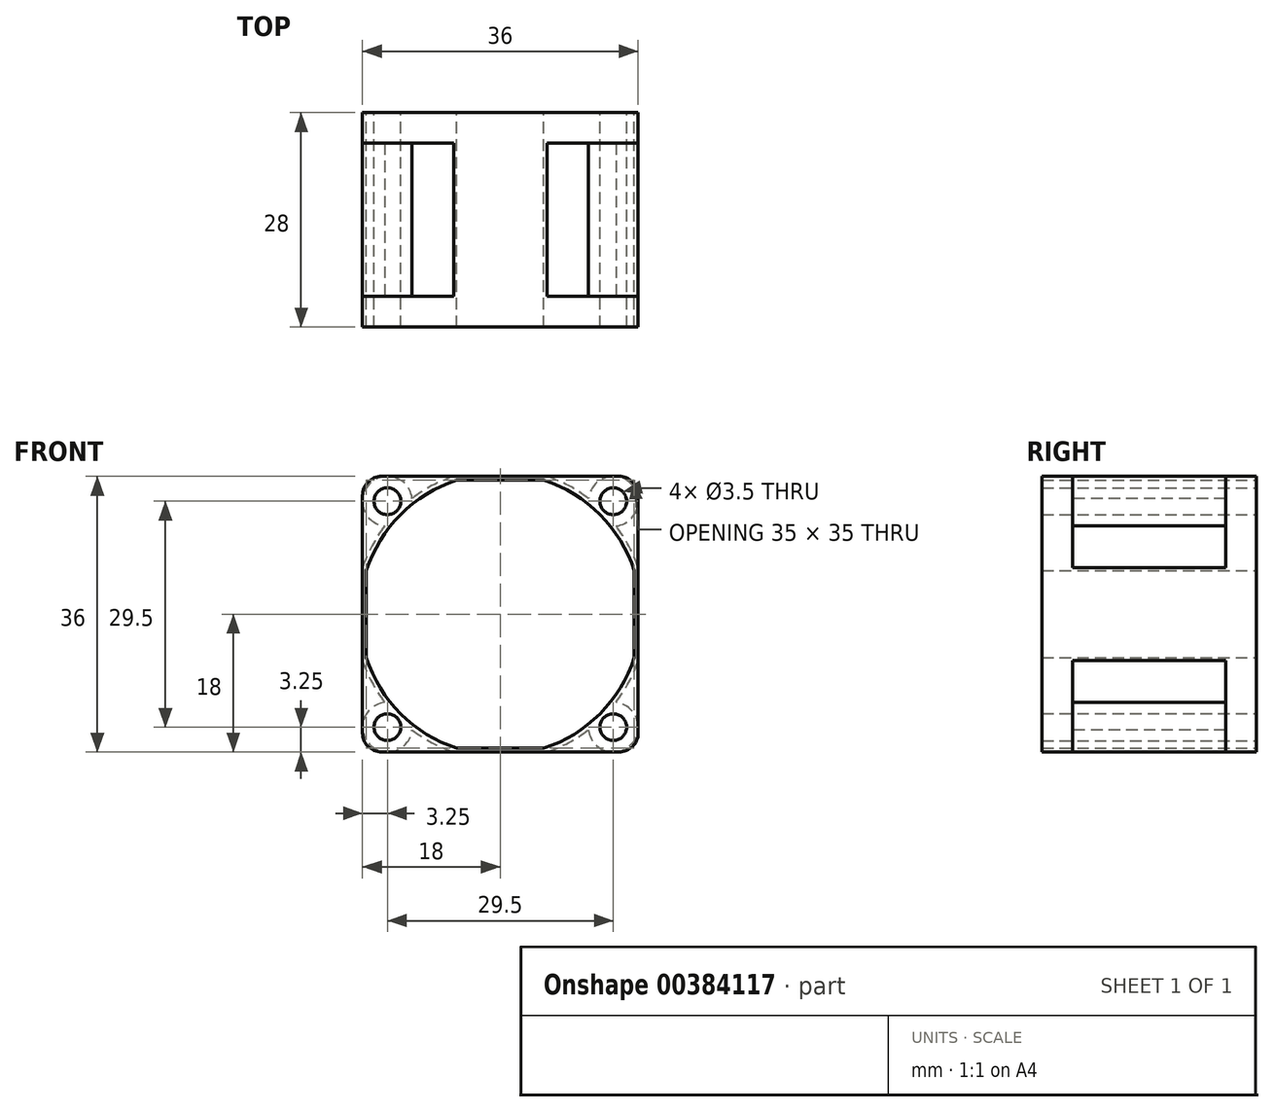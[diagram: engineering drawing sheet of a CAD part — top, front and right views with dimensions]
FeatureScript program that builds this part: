
annotation { "Feature Type Name" : "Feature", "Feature Type Description" : "" }
export const myFeature = defineFeature(function(context is Context, id is Id, definition is map)
    precondition{}
    {
        {
            var Q0;
            Q0=qCreatedBy(makeId("Front.planeOp"),FACE);
            var sketch = newSketch(context, id + "F0", { "sketchPlane" : qUnion([Q0])});
            skLineSegment(sketch, "E0.bottom", {"start": v(-18, 18) * mm, "end": v(18, 18) * mm});
            skLineSegment(sketch, "E0.top", {"start": v(-18, -18) * mm, "end": v(18, -18) * mm});
            skLineSegment(sketch, "E0.left", {"start": v(-18, 18) * mm, "end": v(-18, -18) * mm});
            skLineSegment(sketch, "E0.right", {"start": v(18, 18) * mm, "end": v(18, -18) * mm});
            skArc(sketch, "E1", {"start": v(-5.68, 17.5) * mm, "mid": v(-13.01, 13.01) * mm, "end": v(-17.5, 5.68) * mm});
            skCircle(sketch, "E2", {"center": v(0, 0) * mm, "radius": 17.5 * mm, "construction": true});
            skLineSegment(sketch, "E3", {"start": v(0, 22.42) * mm, "end": v(0, -25.75) * mm, "construction": true});
            skLineSegment(sketch, "E4", {"start": v(-21.61, 0) * mm, "end": v(23.43, 0) * mm, "construction": true});
            skLineSegment(sketch, "E5", {"start": v(-22.47, 22.47) * mm, "end": v(21.99, -21.99) * mm, "construction": true});
            skLineSegment(sketch, "E6", {"start": v(22.36, 22.36) * mm, "end": v(-20.46, -20.46) * mm, "construction": true});
            skCircle(sketch, "E7", {"center": v(-14.75, 14.75) * mm, "radius": 1.75 * mm});
            skCircle(sketch, "E8", {"center": v(14.75, 14.75) * mm, "radius": 1.75 * mm});
            skCircle(sketch, "E9", {"center": v(14.75, -14.75) * mm, "radius": 1.75 * mm});
            skCircle(sketch, "E10", {"center": v(-14.75, -14.75) * mm, "radius": 1.75 * mm});
            skLineSegment(sketch, "E11", {"start": v(-5.68, 17.5) * mm, "end": v(5.68, 17.5) * mm});
            skLineSegment(sketch, "E12", {"start": v(-5.68, -17.5) * mm, "end": v(5.68, -17.5) * mm});
            skLineSegment(sketch, "E13", {"start": v(17.5, 5.68) * mm, "end": v(17.5, -5.68) * mm});
            skLineSegment(sketch, "E14", {"start": v(-17.5, 5.68) * mm, "end": v(-17.5, -5.68) * mm});
            skArc(sketch, "E15.trimOffspring", {"start": v(-17.5, -5.68) * mm, "mid": v(-13.01, -13.01) * mm, "end": v(-5.68, -17.5) * mm});
            skArc(sketch, "E16.trimOffspring", {"start": v(5.68, -17.5) * mm, "mid": v(13.01, -13.01) * mm, "end": v(17.5, -5.68) * mm});
            skArc(sketch, "E17.trimOffspring", {"start": v(17.5, 5.68) * mm, "mid": v(13.01, 13.01) * mm, "end": v(5.68, 17.5) * mm});
            skSolve(sketch);
        }
        {
            var Q0;
            Q0 = qSketchRegion(id + "F0", true);
            extrude(context, id + "F1", {"entities" : qUnion([Q0]), "depth" : 28 * mm, "symmetric" : true});
        }
        {
            var Q0;
            Q0=qCreatedBy(makeId("Front.planeOp"),FACE);
            var sketch = newSketch(context, id + "F2", { "sketchPlane" : qUnion([Q0])});
            skArc(sketch, "E18", {"start": v(-11.52, 15.1) * mm, "mid": v(-17.05, 17.05) * mm, "end": v(-15.1, 11.52) * mm});
            skArc(sketch, "E19", {"start": v(-15.1, 11.52) * mm, "mid": v(-16.78, 8.92) * mm, "end": v(-18, 6.08) * mm});
            skLineSegment(sketch, "E20", {"start": v(19, 19) * mm, "end": v(6.08, 19) * mm});
            skLineSegment(sketch, "E21", {"start": v(-19, 19) * mm, "end": v(-19, 6.08) * mm});
            skLineSegment(sketch, "E22", {"start": v(-19, -19) * mm, "end": v(-6.08, -19) * mm});
            skLineSegment(sketch, "E23", {"start": v(19, -19) * mm, "end": v(19, -6.08) * mm});
            skArc(sketch, "E24", {"start": v(15.1, 11.52) * mm, "mid": v(17.05, 17.05) * mm, "end": v(11.52, 15.1) * mm});
            skArc(sketch, "E25", {"start": v(11.52, -15.1) * mm, "mid": v(17.05, -17.05) * mm, "end": v(15.1, -11.52) * mm});
            skArc(sketch, "E26", {"start": v(-15.1, -11.52) * mm, "mid": v(-17.05, -17.05) * mm, "end": v(-11.52, -15.1) * mm});
            skArc(sketch, "E27.trimOffspring", {"start": v(11.52, 15.1) * mm, "mid": v(8.92, 16.78) * mm, "end": v(6.08, 18) * mm});
            skArc(sketch, "E28.trimOffspring", {"start": v(15.1, -11.52) * mm, "mid": v(16.78, -8.92) * mm, "end": v(18, -6.08) * mm});
            skArc(sketch, "E29.trimOffspring", {"start": v(-11.52, -15.1) * mm, "mid": v(-8.92, -16.78) * mm, "end": v(-6.08, -18) * mm});
            skLineSegment(sketch, "E30", {"start": v(-6.08, 18) * mm, "end": v(-6.08, 19) * mm});
            skLineSegment(sketch, "E31", {"start": v(6.08, 18) * mm, "end": v(6.08, 19) * mm});
            skLineSegment(sketch, "E32", {"start": v(-18, 6.08) * mm, "end": v(-19, 6.08) * mm});
            skLineSegment(sketch, "E33", {"start": v(-18, -6.08) * mm, "end": v(-19, -6.08) * mm});
            skLineSegment(sketch, "E34", {"start": v(18, 6.08) * mm, "end": v(19, 6.08) * mm});
            skLineSegment(sketch, "E35", {"start": v(18, -6.08) * mm, "end": v(19, -6.08) * mm});
            skLineSegment(sketch, "E36", {"start": v(-6.08, -18) * mm, "end": v(-6.08, -19) * mm});
            skLineSegment(sketch, "E37", {"start": v(6.08, -18) * mm, "end": v(6.08, -19) * mm});
            skArc(sketch, "E38.trimOffspring", {"start": v(-18, -6.08) * mm, "mid": v(-16.78, -8.92) * mm, "end": v(-15.1, -11.52) * mm});
            skLineSegment(sketch, "E39.trimOffspring", {"start": v(-19, -6.08) * mm, "end": v(-19, -19) * mm});
            skLineSegment(sketch, "E40.trimOffspring", {"start": v(6.08, -19) * mm, "end": v(19, -19) * mm});
            skArc(sketch, "E41.trimOffspring", {"start": v(6.08, -18) * mm, "mid": v(8.92, -16.78) * mm, "end": v(11.52, -15.1) * mm});
            skLineSegment(sketch, "E42.trimOffspring", {"start": v(19, 6.08) * mm, "end": v(19, 19) * mm});
            skArc(sketch, "E43.trimOffspring", {"start": v(18, 6.08) * mm, "mid": v(16.78, 8.92) * mm, "end": v(15.1, 11.52) * mm});
            skLineSegment(sketch, "E44.trimOffspring", {"start": v(-6.08, 19) * mm, "end": v(-19, 19) * mm});
            skArc(sketch, "E45.trimOffspring", {"start": v(-6.08, 18) * mm, "mid": v(-8.92, 16.78) * mm, "end": v(-11.52, 15.1) * mm});
            skSolve(sketch);
        }
        {
            var Q0;
            Q0 = qSketchRegion(id + "F2", true);
            extrude(context, id + "F3", {"entities" : qUnion([Q0]), "operationType" : NewBodyOperationType.REMOVE, "oppositeDirection" : true, "depth" : 20 * mm, "symmetric" : true});
        }
        {
            var Q0;
            {var subQ0=sQuery(id+"F0.wireOp",EDGE,"E0.bottom");var subQ1=sQuery(id+"F0.wireOp",EDGE,"E0.right");Q0=makeQuery(id+"F3.boolean.opBoolean","SPLIT",EDGE,{"disambiguationData":[TD([makeQuery(id+"F3.opExtrude","CAP_FACE",FACE,{"disambiguationData":[OSD([sQuery(id+"F2.wireOp",EDGE,"E20"),sQuery(id+"F2.wireOp",EDGE,"E24"),sQuery(id+"F2.wireOp",EDGE,"E27.trimOffspring"),sQuery(id+"F2.wireOp",EDGE,"E31"),sQuery(id+"F2.wireOp",EDGE,"E34"),sQuery(id+"F2.wireOp",EDGE,"E42.trimOffspring"),sQuery(id+"F2.wireOp",EDGE,"E43.trimOffspring")])],"isStart":true})])],"derivedFrom":makeQuery(id+"F1.opExtrude","SWEPT_EDGE",EDGE,{"disambiguationData":[OSD([subQ0,subQ1])]})});}
            var Q1;
            {var subQ0=sQuery(id+"F0.wireOp",EDGE,"E0.bottom");var subQ1=sQuery(id+"F0.wireOp",EDGE,"E0.right");Q1=makeQuery(id+"F3.boolean.opBoolean","SPLIT",EDGE,{"disambiguationData":[TD([makeQuery(id+"F3.opExtrude","CAP_FACE",FACE,{"disambiguationData":[OSD([sQuery(id+"F2.wireOp",EDGE,"E20"),sQuery(id+"F2.wireOp",EDGE,"E24"),sQuery(id+"F2.wireOp",EDGE,"E27.trimOffspring"),sQuery(id+"F2.wireOp",EDGE,"E31"),sQuery(id+"F2.wireOp",EDGE,"E34"),sQuery(id+"F2.wireOp",EDGE,"E42.trimOffspring"),sQuery(id+"F2.wireOp",EDGE,"E43.trimOffspring")])],"isStart":false})])],"derivedFrom":makeQuery(id+"F1.opExtrude","SWEPT_EDGE",EDGE,{"disambiguationData":[OSD([subQ0,subQ1])]})});}
            var Q2;
            {var subQ0=sQuery(id+"F0.wireOp",EDGE,"E0.right");var subQ1=sQuery(id+"F0.wireOp",EDGE,"E0.top");Q2=makeQuery(id+"F3.boolean.opBoolean","SPLIT",EDGE,{"disambiguationData":[TD([makeQuery(id+"F3.opExtrude","CAP_FACE",FACE,{"disambiguationData":[OSD([sQuery(id+"F2.wireOp",EDGE,"E23"),sQuery(id+"F2.wireOp",EDGE,"E25"),sQuery(id+"F2.wireOp",EDGE,"E28.trimOffspring"),sQuery(id+"F2.wireOp",EDGE,"E35"),sQuery(id+"F2.wireOp",EDGE,"E37"),sQuery(id+"F2.wireOp",EDGE,"E40.trimOffspring"),sQuery(id+"F2.wireOp",EDGE,"E41.trimOffspring")])],"isStart":true})])],"derivedFrom":makeQuery(id+"F1.opExtrude","SWEPT_EDGE",EDGE,{"disambiguationData":[OSD([subQ1,subQ0])]})});}
            var Q3;
            {var subQ0=sQuery(id+"F0.wireOp",EDGE,"E0.right");var subQ1=sQuery(id+"F0.wireOp",EDGE,"E0.top");Q3=makeQuery(id+"F3.boolean.opBoolean","SPLIT",EDGE,{"disambiguationData":[TD([makeQuery(id+"F3.opExtrude","CAP_FACE",FACE,{"disambiguationData":[OSD([sQuery(id+"F2.wireOp",EDGE,"E23"),sQuery(id+"F2.wireOp",EDGE,"E25"),sQuery(id+"F2.wireOp",EDGE,"E28.trimOffspring"),sQuery(id+"F2.wireOp",EDGE,"E35"),sQuery(id+"F2.wireOp",EDGE,"E37"),sQuery(id+"F2.wireOp",EDGE,"E40.trimOffspring"),sQuery(id+"F2.wireOp",EDGE,"E41.trimOffspring")])],"isStart":false})])],"derivedFrom":makeQuery(id+"F1.opExtrude","SWEPT_EDGE",EDGE,{"disambiguationData":[OSD([subQ1,subQ0])]})});}
            var Q4;
            {var subQ0=sQuery(id+"F0.wireOp",EDGE,"E0.bottom");var subQ1=sQuery(id+"F0.wireOp",EDGE,"E0.left");Q4=makeQuery(id+"F3.boolean.opBoolean","SPLIT",EDGE,{"disambiguationData":[TD([makeQuery(id+"F3.opExtrude","CAP_FACE",FACE,{"disambiguationData":[OSD([sQuery(id+"F2.wireOp",EDGE,"E18"),sQuery(id+"F2.wireOp",EDGE,"E19"),sQuery(id+"F2.wireOp",EDGE,"E21"),sQuery(id+"F2.wireOp",EDGE,"E30"),sQuery(id+"F2.wireOp",EDGE,"E32"),sQuery(id+"F2.wireOp",EDGE,"E44.trimOffspring"),sQuery(id+"F2.wireOp",EDGE,"E45.trimOffspring")])],"isStart":true})])],"derivedFrom":makeQuery(id+"F1.opExtrude","SWEPT_EDGE",EDGE,{"disambiguationData":[OSD([subQ0,subQ1])]})});}
            var Q5;
            {var subQ0=sQuery(id+"F0.wireOp",EDGE,"E0.bottom");var subQ1=sQuery(id+"F0.wireOp",EDGE,"E0.left");Q5=makeQuery(id+"F3.boolean.opBoolean","SPLIT",EDGE,{"disambiguationData":[TD([makeQuery(id+"F3.opExtrude","CAP_FACE",FACE,{"disambiguationData":[OSD([sQuery(id+"F2.wireOp",EDGE,"E18"),sQuery(id+"F2.wireOp",EDGE,"E19"),sQuery(id+"F2.wireOp",EDGE,"E21"),sQuery(id+"F2.wireOp",EDGE,"E30"),sQuery(id+"F2.wireOp",EDGE,"E32"),sQuery(id+"F2.wireOp",EDGE,"E44.trimOffspring"),sQuery(id+"F2.wireOp",EDGE,"E45.trimOffspring")])],"isStart":false})])],"derivedFrom":makeQuery(id+"F1.opExtrude","SWEPT_EDGE",EDGE,{"disambiguationData":[OSD([subQ0,subQ1])]})});}
            var Q6;
            {var subQ0=sQuery(id+"F0.wireOp",EDGE,"E0.left");var subQ1=sQuery(id+"F0.wireOp",EDGE,"E0.top");Q6=makeQuery(id+"F3.boolean.opBoolean","SPLIT",EDGE,{"disambiguationData":[TD([makeQuery(id+"F3.opExtrude","CAP_FACE",FACE,{"disambiguationData":[OSD([sQuery(id+"F2.wireOp",EDGE,"E22"),sQuery(id+"F2.wireOp",EDGE,"E26"),sQuery(id+"F2.wireOp",EDGE,"E29.trimOffspring"),sQuery(id+"F2.wireOp",EDGE,"E33"),sQuery(id+"F2.wireOp",EDGE,"E36"),sQuery(id+"F2.wireOp",EDGE,"E38.trimOffspring"),sQuery(id+"F2.wireOp",EDGE,"E39.trimOffspring")])],"isStart":false})])],"derivedFrom":makeQuery(id+"F1.opExtrude","SWEPT_EDGE",EDGE,{"disambiguationData":[OSD([subQ1,subQ0])]})});}
            var Q7;
            {var subQ0=sQuery(id+"F0.wireOp",EDGE,"E0.left");var subQ1=sQuery(id+"F0.wireOp",EDGE,"E0.top");Q7=makeQuery(id+"F3.boolean.opBoolean","SPLIT",EDGE,{"disambiguationData":[TD([makeQuery(id+"F3.opExtrude","CAP_FACE",FACE,{"disambiguationData":[OSD([sQuery(id+"F2.wireOp",EDGE,"E22"),sQuery(id+"F2.wireOp",EDGE,"E26"),sQuery(id+"F2.wireOp",EDGE,"E29.trimOffspring"),sQuery(id+"F2.wireOp",EDGE,"E33"),sQuery(id+"F2.wireOp",EDGE,"E36"),sQuery(id+"F2.wireOp",EDGE,"E38.trimOffspring"),sQuery(id+"F2.wireOp",EDGE,"E39.trimOffspring")])],"isStart":true})])],"derivedFrom":makeQuery(id+"F1.opExtrude","SWEPT_EDGE",EDGE,{"disambiguationData":[OSD([subQ1,subQ0])]})});}
            fillet(context, id + "F4", {"entities" : qUnion([Q0, Q1, Q2, Q3, Q4, Q5, Q6, Q7]), "radius" : 2.5 * mm, "tangentPropagation" : true, "allowEdgeOverflow" : false});
        }
    });
